# Revit family: Kühlplatte stille Kühlung GN1-1 - Eigen
name_source: partatom
category: Sonderausstattung
revit_build: Autodesk Revit 2015 (Build: 20140606_1530(x64)
units: mm (PartAtom-declared; Revit-internal decimal feet)

## types (4) — shared parameters
Artikelnr. = KPMS021100
Boden Stärke = 60 mm  [stored 0.19685 ft]
Breite Technikgehäuse = 441 mm
DN Tauwasserabfluß = 25 mm  [stored 0.082021 ft]
Höhe = 530 mm
Höhe Technikgehäuse = 400 mm  [stored 1.31234 ft]
Höhe Unterbau = 50 mm  [stored 0.164042 ft]
Höhe Wanne = 80 mm  [stored 0.262467 ft]
Kapazität = 2 x GN 1/1, Tiefe 20 mm
Kälteleistung = 1050 W / -10°C VT
Kältemittel = R404a
Material = Edelstahl AISI 304
Pole = 1
Rand Breite hinten = 63 mm
Rand Breite seitlich = 88 mm
Rand Breite vorne = 63 mm
Rand Stärke = 9 mm  [stored 0.0295276 ft]
Scheinleistung = 0 VA
Spannung = 230 V
Temp. Bereich = -10°C bis 0°C
Tiefe = 635 mm
Tiefe ohne Rahmen = 590 mm
Wand Seiten Stärke = 66 mm
Wand hinten Stärke = 40 mm
Wand vorne Stärke = 40 mm

## per-type parameters (varying)
| type | Breite | Breite ohne Rahmen | Watt |
| 2xGN1-1 | 805 mm  [stored 2.64108 ft] | 761 mm | 500 W |
| 3xGN1-1 | 1135 mm | 1091 mm | 500 W |
| 4xGN1-1 | 1455 mm | 1411 mm | 500 W |
| 5xGN1-1 | 1780 mm | 1736 mm | 600 W |

note: [stored X ft] marks values corroborated as IEEE doubles in the binary element streams (Revit-internal decimal feet)

## geometry (parser evidence)
native form markers: Blend x14, Sweep x3
no freeform markers — native parametric forms only
